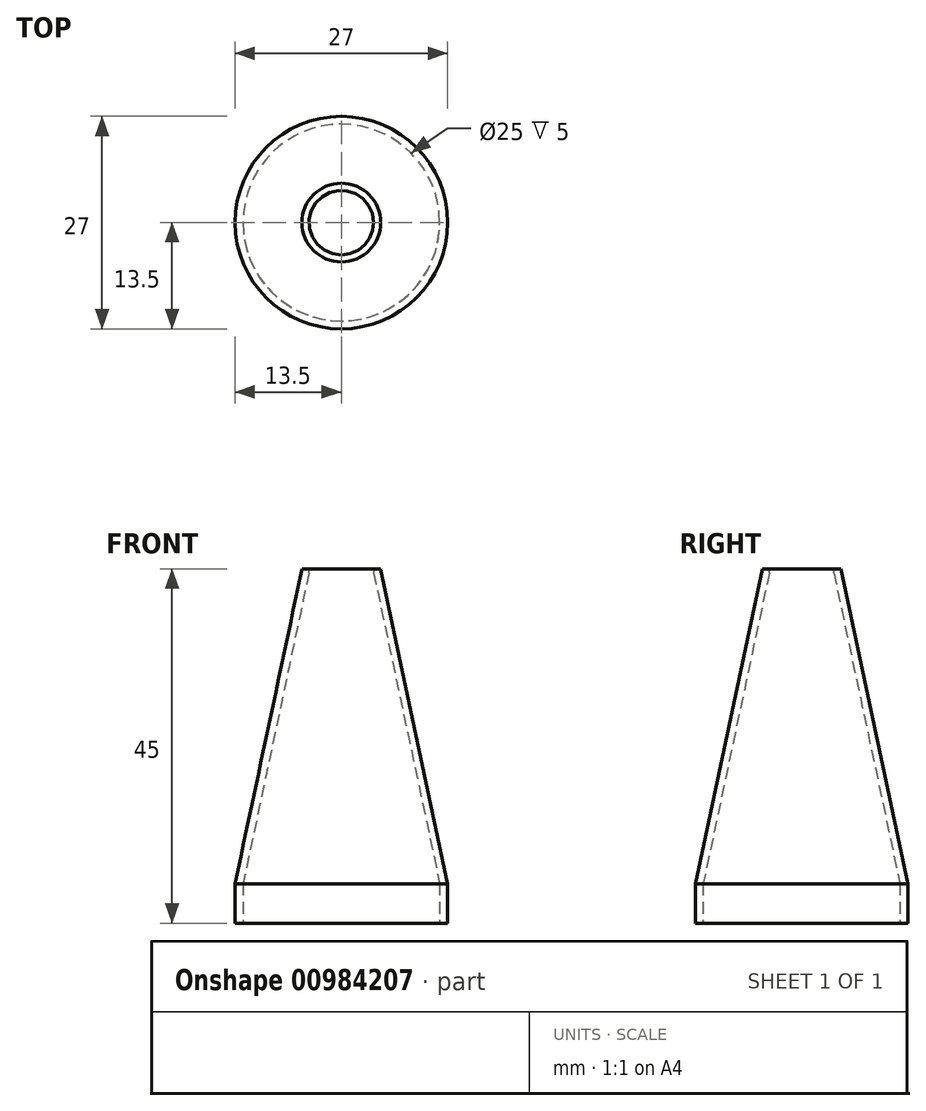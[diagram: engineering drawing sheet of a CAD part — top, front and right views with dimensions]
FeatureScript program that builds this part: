
annotation { "Feature Type Name" : "Feature", "Feature Type Description" : "" }
export const myFeature = defineFeature(function(context is Context, id is Id, definition is map)
    precondition{}
    {
        {
            var Q0;
            Q0=qCreatedBy(makeId("Top.planeOp"),FACE);
            var sketch = newSketch(context, id + "F0", { "sketchPlane" : qUnion([Q0])});
            skCircle(sketch, "E0", {"center": v(0, 0) * mm, "radius": 12.5 * mm});
            skCircle(sketch, "E1.0", {"center": v(0, 0) * mm, "radius": 13.5 * mm});
            skSolve(sketch);
        }
        {
            var Q0;
            Q0=qCreatedBy(makeId("Top.planeOp"),FACE);
            cPlane(context, id + "F1", {"entities" : qUnion([Q0]), "cplaneType" : CPlaneType.OFFSET, "offset" : 45 * mm, "width" : 150 * mm, "height" : 150 * mm});
        }
        {
            var Q0;
            Q0=makeQuery(id+"F0.imprint","IMPRINT",FACE,{"disambiguationData":[TD([[makeQuery(id+"F0.imprint","IMPRINT",EDGE,{"derivedFrom":sQuery(id+"F0.wireOp",EDGE,"E0")}),-1.0]])]});
            extrude(context, id + "F2", {"entities" : qUnion([Q0]), "depth" : 5 * mm, "offsetDistance" : 25 * mm});
        }
        {
            var Q0;
            Q0=qCreatedBy(id+"F1.planeOp",FACE);
            var sketch = newSketch(context, id + "F3", { "sketchPlane" : qUnion([Q0])});
            skCircle(sketch, "E2", {"center": v(0, 0) * mm, "radius": 4 * mm});
            skCircle(sketch, "E3.0", {"center": v(0, 0) * mm, "radius": 5 * mm});
            skSolve(sketch);
        }
        {
            var Q0;
            Q0=qCreatedBy(makeId("Front.planeOp"),FACE);
            var sketch = newSketch(context, id + "F4", { "sketchPlane" : qUnion([Q0])});
            skLineSegment(sketch, "E4.0", {"start": v(-5, 45) * mm, "end": v(5, 45) * mm});
            skLineSegment(sketch, "E5.0", {"start": v(-13.5, 5) * mm, "end": v(13.5, 5) * mm});
            skLineSegment(sketch, "E6.0", {"start": v(-12.5, 5) * mm, "end": v(12.5, 5) * mm});
            skLineSegment(sketch, "E7.0", {"start": v(-4, 45) * mm, "end": v(4, 45) * mm});
            skLineSegment(sketch, "E8", {"start": v(-5, 45) * mm, "end": v(-13.5, 5) * mm});
            skLineSegment(sketch, "E9", {"start": v(-12.5, 5) * mm, "end": v(-4, 45) * mm});
            skSolve(sketch);
        }
        {
            var Q0;
            {var subQ0=sQuery(id+"F4.wireOp",EDGE,"E8");Q0=makeQuery(id+"F4.imprint","IMPRINT",FACE,{"disambiguationData":[TD([[makeQuery(id+"F4.imprint","IMPRINT",EDGE,{"derivedFrom":subQ0}),1.0]])]});}
            var Q1;
            Q1=sQuery(id+"F3.wireOp",EDGE,"E2");
            revolve(context, id + "F5", {"operationType" : NewBodyOperationType.ADD, "surfaceOperationType" : NewSurfaceOperationType.NEW, "entities" : qUnion([Q0]), "axis" : qUnion([Q1]), "revolveType" : RevolveType.FULL});
        }
        {
            var Q0;
            Q0=makeQuery(id+"F5.opRevolve","SWEPT_EDGE",EDGE,{"disambiguationData":[OSD([sQuery(id+"F4.wireOp",EDGE,"E4.0"),sQuery(id+"F4.wireOp",EDGE,"E9")])]});
            fillet(context, id + "F6", {"entities" : qUnion([Q0]), "radius" : 0.4 * mm, "tangentPropagation" : true, "allowEdgeOverflow" : false});
        }
    });
